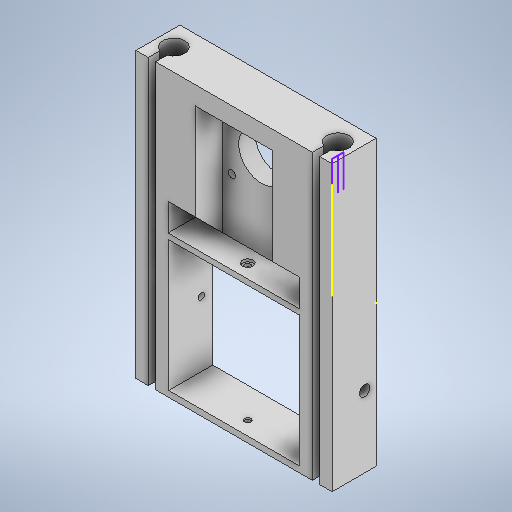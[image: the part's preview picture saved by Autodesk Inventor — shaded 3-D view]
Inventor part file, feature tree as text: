
AUTODESK INVENTOR PART (.ipt)
format: ipt  version: 2025 (Build 290162000, 162)  size: 426,496 bytes
history: native  units: in
note: dims shown in document units (in); Inventor stores cm internally (conversion verified against a paired STEP export)
features: sketch x16, extrude x15
ambient origin geometry x8: Origin, YZ Plane, XZ Plane, XY Plane, X Axis, Y Axis, Z Axis, Center Point
bodies: Solid1 (feature_tree)
feature tree (31):
  extrude  "Extrusion1"  Depth=0.7087in
  extrude  "Extrusion2"  Depth=0.2559in
  extrude  "Extrusion3"  Depth=0.9449in TaperAngle=0.0deg
  extrude  "Extrusion4"  Depth=0.5906in TaperAngle=0.0deg
  extrude  "Extrusion5"  Depth=0.689in
  extrude  "Extrusion6"  Depth=0.4724in
  extrude  "Extrusion7"  Depth=0.3937in
  extrude  "Extrusion9"  Depth=1.6614in
  extrude  "Extrusion8"  Depth=0.5906in TaperAngle=0.0deg
  sketch  "Sketch14"  dims[d23=0.8307in d24=0.9843in]
  extrude  "Extrusion10"  Depth=0.9843in
  extrude  "Extrusion11"  Depth=0.1575in
  extrude  "Extrusion12"  TaperAngle=135.0deg  [1 undecoded]
  extrude  "Extrusion13"  Depth=0.5866in TaperAngle=0.0deg
  extrude  "Extrusion14"  Depth=0.5866in
  extrude  "Extrusion15"  Depth=6.1024in
  sketch  "Sketch1"  dims[d0=2.7953in d1=0.7087in]
  sketch  "Sketch2"  dims[d2=0.7087in d3=0.2559in]
  sketch  "Sketch3"  dims[d4=0.2559in d5=0.9449in d6=0.0in]
  sketch  "Sketch4"  dims[d7=2.8346in d8=0.5906in d9=0.0in]
  sketch  "Sketch5"  dims[d10=0.689in d11=0.689in]
  sketch  "Sketch7"  dims[d12=0.4724in d14=0.4724in]
  sketch  "Sketch8"  dims[d15=47.2441in d16=0.0in d17=0.3937in]
  sketch  "Sketch10"  dims[d18=0.8307in d19=1.6614in]
  sketch  "Sketch11"  dims[d20=1.6614in d21=0.5906in d22=0.0in]
  sketch  "Sketch15"  dims[d25=0.2784in d26=0.1575in]
  sketch  "Sketch16"  dims[d30=1.378in d31=0.0in d32=135.0deg]
  sketch  "Sketch17"  dims[d33=0.5866in d34=0.5866in d35=0.0in]
  sketch  "Sketch18"  dims[d36=45.0deg d37=0.5866in]
  sketch  "Sketch19"  dims[d38=0.5866in d39=0.0in d42=6.1024in]
  sketch  "Sketch20"  dims[d43=6.1024in d44=6.1024in d49=0.1575in d50=0.1575in d51=0.1575in d52=3.3465in d53=2.8047in d54=2.8047in d55=13.1102in d56=0.0in d57=0.5906in d58=0.0in d59=0.1575in d60=0.1575in d61=0.5in d62=0.1378in d63=39.3701in d64=0.0in d65=0.5in d66=0.2264in d67=0.5906in d68=0.0in d69=0.2264in d70=0.5906in d71=0.0in d72=0.1378in d73=3.937in d74=0.0in d75=0.2264in d76=0.0551in d77=0.0in d78=0.0945in d79=0.0in]
note: 1 required parameter value undecoded (feature->parameter linkage not recoverable at this tier; creation-order binding heuristic only, values carry confidence <= 0.55)
